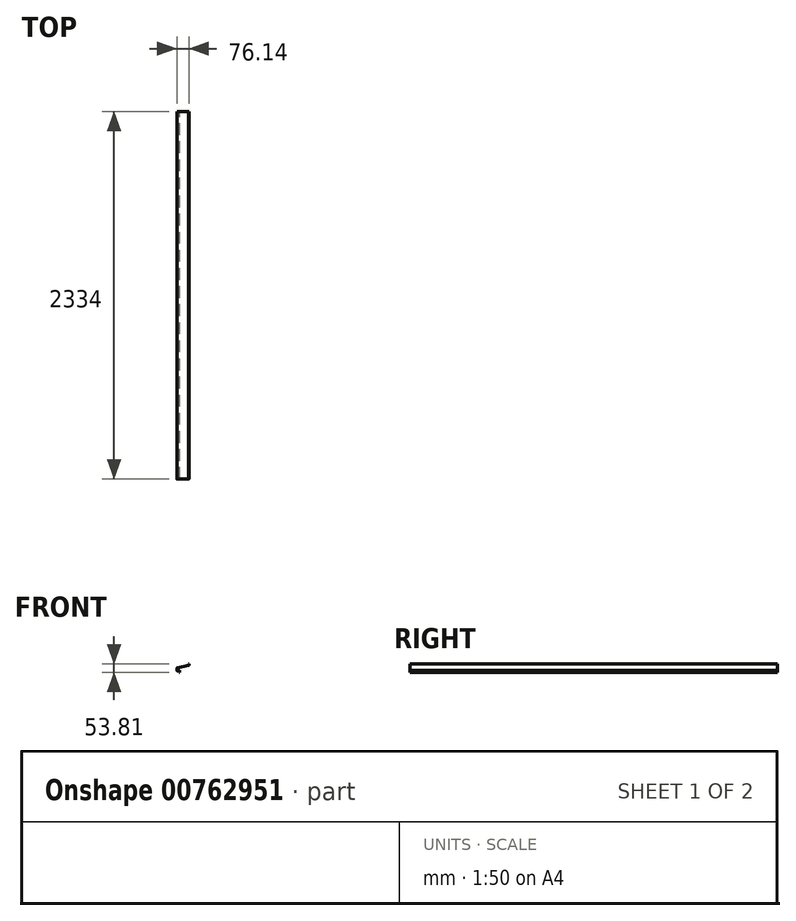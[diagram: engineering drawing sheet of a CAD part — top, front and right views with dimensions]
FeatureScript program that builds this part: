
annotation { "Feature Type Name" : "Feature", "Feature Type Description" : "" }
export const myFeature = defineFeature(function(context is Context, id is Id, definition is map)
    precondition{}
    {
        {
            var Q0;
            Q0=qCreatedBy(makeId("Front.planeOp"),FACE);
            var sketch = newSketch(context, id + "F0", { "sketchPlane" : qUnion([Q0])});
            skLineSegment(sketch, "E0", {"start": v(0, 0) * mm, "end": v(0, 10) * mm});
            skLineSegment(sketch, "E1", {"start": v(-1, 11) * mm, "end": v(-14, 11) * mm});
            skLineSegment(sketch, "E2", {"start": v(-15, 12) * mm, "end": v(-15, 27.2) * mm});
            skLineSegment(sketch, "E3", {"start": v(-14.22, 28.17) * mm, "end": v(59.36, 44.63) * mm});
            skLineSegment(sketch, "E4", {"start": v(60.14, 45.6) * mm, "end": v(60.14, 53.8) * mm});
            skPoint(sketch, "E5.visualSharp", {"position": v(0, 11) * mm});
            skArc(sketch, "E5.filletArc", {"start": v(0, 10) * mm, "mid": v(-0.3, 10.7) * mm, "end": v(-1, 11) * mm});
            skPoint(sketch, "E6.visualSharp", {"position": v(-15, 11) * mm});
            skArc(sketch, "E6.filletArc", {"start": v(-15, 12) * mm, "mid": v(-14.7, 11.3) * mm, "end": v(-14, 11) * mm});
            skPoint(sketch, "E7.visualSharp", {"position": v(-15, 28) * mm});
            skArc(sketch, "E7.filletArc", {"start": v(-14.22, 28.17) * mm, "mid": v(-14.78, 27.82) * mm, "end": v(-15, 27.2) * mm});
            skPoint(sketch, "E8.visualSharp", {"position": v(60.14, 44.8) * mm});
            skArc(sketch, "E8.filletArc", {"start": v(59.36, 44.63) * mm, "mid": v(59.92, 44.98) * mm, "end": v(60.14, 45.6) * mm});
            skLineSegment(sketch, "E9.0", {"start": v(61.14, 45.6) * mm, "end": v(61.14, 53.8) * mm});
            skArc(sketch, "E9.1", {"start": v(59.58, 43.66) * mm, "mid": v(60.7, 44.36) * mm, "end": v(61.14, 45.6) * mm});
            skLineSegment(sketch, "E9.2", {"start": v(-13.22, 27.37) * mm, "end": v(59.58, 43.66) * mm});
            skLineSegment(sketch, "E9.3", {"start": v(1, 0) * mm, "end": v(1, 10) * mm});
            skArc(sketch, "E9.4", {"start": v(1, 10) * mm, "mid": v(0.41, 11.41) * mm, "end": v(-1, 12) * mm});
            skLineSegment(sketch, "E9.5", {"start": v(-1, 12) * mm, "end": v(-13, 12) * mm});
            skLineSegment(sketch, "E9.6", {"start": v(-14, 13) * mm, "end": v(-14, 26.4) * mm});
            skLineSegment(sketch, "E10", {"start": v(60.14, 53.8) * mm, "end": v(61.14, 53.8) * mm});
            skLineSegment(sketch, "E11", {"start": v(1, 0) * mm, "end": v(0, 0) * mm});
            skArc(sketch, "E12.filletArc", {"start": v(-14, 13) * mm, "mid": v(-13.7, 12.3) * mm, "end": v(-13, 12) * mm});
            skArc(sketch, "E13.filletArc", {"start": v(-13.22, 27.37) * mm, "mid": v(-13.78, 27.02) * mm, "end": v(-14, 26.4) * mm});
            skSolve(sketch);
        }
        {
            var Q0;
            Q0=makeQuery(id+"F0.imprint","IMPRINT",FACE,{"disambiguationData":[TD([[makeQuery(id+"F0.imprint","IMPRINT",EDGE,{"derivedFrom":sQuery(id+"F0.wireOp",EDGE,"E0")}),-1.0]])]});
            extrude(context, id + "F1", {"entities" : qUnion([Q0]), "depth" : 2334 * mm, "offsetDistance" : 25 * mm});
        }
    });
